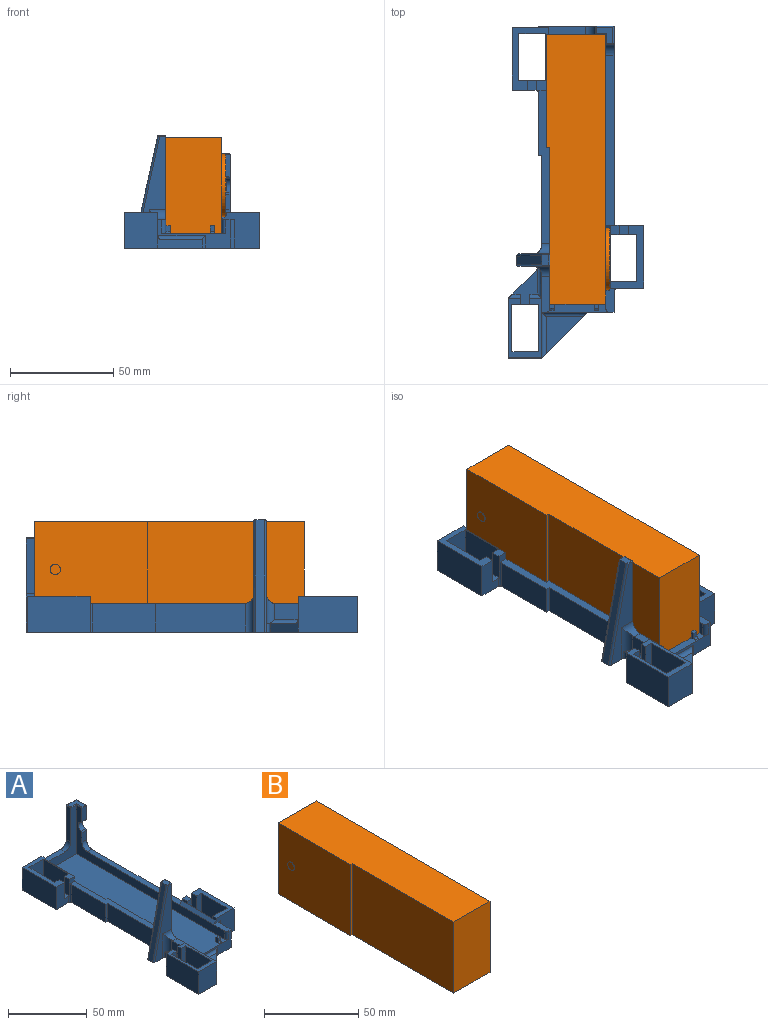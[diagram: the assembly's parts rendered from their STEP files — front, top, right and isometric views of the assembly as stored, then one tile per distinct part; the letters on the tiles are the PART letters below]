
ASSEMBLY  parts=2 mates=1
PART A: 117 faces, bbox 65.6x160.9x54.8 mm
  f0: plane 82.48x4mm, normal (0,0,1), area 329.9mm2, adj f1,f28,f41,f115
  f1: plane 96.48x45.15mm, normal (1,0,0), area 1595mm2, adj f0,f27,f31,f32,f38,f41,f47,f53
  f2: plane 17.5x11.5mm, normal (0,-1,0), area 148.3mm2, adj f4,f32,f57,f111,f113,f114
  f3: plane 12.75x4.56mm, normal (-1,0,0), area 57.9mm2, adj f5,f57,f59,f112,f113,f114
  f4: plane 12.75x4.5mm, normal (1,0,0), area 57.4mm2, adj f2,f57,f59,f113
  f5: plane 74.33x6.35mm, normal (0,0,1), area 304.3mm2, adj f3,f6,f25,f29,f30,f33,f34,f42
  f6: plane 30.85x13.75mm, normal (-1,0,0), area 424.1mm2, adj f5,f29,f32,f114
  f7: cylinder r=1mm len=54.65mm, axis (0.22,0,0.98), area 87.2mm2, adj f32,f35,f36,f50,f56
  f8: cylinder r=1mm len=54.65mm, axis (0.22,0,0.98), area 87.2mm2, adj f21,f32,f35,f52,f56
  f9: plane 4.5x1.75mm, normal (-1,0,0), area 7.9mm2, adj f11,f64,f107,f115
  f10: plane 3x1.75mm, normal (-1,0,0), area 5.3mm2, adj f12,f13,f63,f107
  f11: plane 4.5x4.15mm, normal (0,0,1), area 18.7mm2, adj f9,f64,f67,f115
  f12: plane 30.5x16mm, normal (0,0,1), area 154.7mm2, adj f10,f13,f63,f64,f65,f68,f115,f116
  f13: plane 18.3x17.5mm, normal (0,-1,0), area 231.4mm2, adj f10,f12,f17,f32,f91,f107,f116
  f14: plane 23x15.75mm, normal (1,0,0), area 362.3mm2, adj f32,f63,f64,f107
  f15: plane 3.75x3.43mm, normal (1,0,0), area 12.8mm2, adj f23,f26,f57,f60
  f16: plane 134.75x31.1mm, normal (0,0,1), area 3733.9mm2, adj f20,f25,f26,f28,f33,f34,f94,f97
  f17: plane 11.78x6mm, normal (0,0,1), area 47.1mm2, adj f13,f20,f22,f28,f91,f106
  f18: plane 17.35x4mm, normal (0,0,1), area 67.5mm2, adj f19,f20,f34,f43,f71,f80,f105
  f19: plane 11.42x7.85mm, normal (-1,0,0), area 88.5mm2, adj f18,f43,f71,f89,f108
  f20: plane 34.95x13.75mm, normal (0,-1,0), area 141mm2, adj f16,f17,f18,f22,f32,f80,f87,f90
  f21: plane 53.9x14.98mm, normal (0,-1,0), area 333.8mm2, adj f8,f32,f34,f43,f52,f108
  f22: plane 13.75x9.78mm, normal (1,0,0), area 134.4mm2, adj f17,f20,f32,f91
  f23: plane 22.8x4mm, normal (0,0,1), area 73.4mm2, adj f15,f24,f26,f31,f40,f60
  f24: plane 13.75x0.58mm, normal (-1,0,0), area 7.9mm2, adj f23,f31,f32,f60
  f25: plane 54.92x10.25mm, normal (1,0,0), area 458.5mm2, adj f5,f16,f26,f33,f57,f112
  f26: plane 37.9x28.8mm, normal (0,-1,0), area 354.1mm2, adj f15,f16,f23,f25,f28,f39,f40,f46
  f27: plane 7.26x4mm, normal (0,-1,0), area 29.1mm2, adj f1,f28,f41,f55
  f28: plane 132.75x37.9mm, normal (-1,0,0), area 1005.7mm2, adj f0,f16,f17,f26,f27,f38,f41,f44
  f29: plane 13.75x1.7mm, normal (0,-1,0), area 23.4mm2, adj f5,f6,f30,f32
  f30: plane 43.48x13.85mm, normal (-1,0,0), area 597.9mm2, adj f5,f29,f32,f42,f109
  f31: plane 45.15x36.8mm, normal (0,1,0), area 794mm2, adj f1,f23,f24,f32,f39,f40,f49
  f32: plane 160.91x65.54mm, normal (0,0,-1), area 5829.9mm2, adj f1,f2,f6,f7,f8,f13,f14,f20
  f33: plane 6.5x1.7mm, normal (0,1,0), area 11.1mm2, adj f5,f16,f25,f34
  f34: plane 77.83x46.65mm, normal (1,0,0), area 750.5mm2, adj f5,f16,f18,f21,f33,f36,f42,f43
  f35: plane 5.01x3.4mm, normal (0,0,1), area 16.9mm2, adj f7,f8,f50,f51,f52,f56
  f36: plane 53.9x14.98mm, normal (0,1,0), area 333.8mm2, adj f7,f32,f34,f42,f50,f109
  f37: plane 8x8mm, normal (0,0,1), area 39mm2, adj f44,f45,f46,f47,f48,f49
  f38: plane 10.36x4mm, normal (0,-1,0), area 41.5mm2, adj f1,f28,f45,f54
  f39: plane 26.4x4mm, normal (-1,0,0), area 105.6mm2, adj f26,f31,f40,f48
  f40: cylinder r=5mm len=5mm, axis (0,-1,0), area 31.4mm2, adj f23,f26,f31,f39
  f41: cylinder r=5mm len=5mm, axis (1,0,0), area 31.4mm2, adj f0,f1,f27,f28
  f42: cylinder r=5mm len=8mm, axis (-1,0,0), area 41.6mm2, adj f5,f30,f34,f36,f109
  f43: cylinder r=5mm len=8mm, axis (1,0,0), area 41.6mm2, adj f18,f19,f21,f34,f108
  f44: cylinder r=0.5mm len=5.5mm, axis (0,1,0), area 3.9mm2, adj f28,f37,f45,f46
  f45: cylinder r=0.5mm len=4mm, axis (-1,0,0), area 2.9mm2, adj f37,f38,f44,f47
  f46: cylinder r=0.5mm len=5.5mm, axis (-1,0,0), area 3.9mm2, adj f26,f37,f44,f48
  f47: cylinder r=0.5mm len=9mm, axis (0,1,0), area 6.8mm2, adj f1,f37,f45,f49
  f48: cylinder r=0.5mm len=4mm, axis (0,1,0), area 2.9mm2, adj f37,f39,f46,f49
  f49: cylinder r=0.5mm len=9mm, axis (-1,0,0), area 6.8mm2, adj f31,f37,f47,f48
  f50: cylinder r=0.5mm len=3.75mm, axis (1,0,0), area 2.5mm2, adj f7,f35,f36,f51
  f51: cylinder r=0.5mm len=6mm, axis (0,-1,0), area 4.4mm2, adj f34,f35,f50,f52
  f52: cylinder r=0.5mm len=3.75mm, axis (-1,0,0), area 2.5mm2, adj f8,f21,f35,f51
  f53: cylinder r=3.5mm len=6.83mm, axis (1,0,0), area 37.7mm2, adj f1,f28,f54,f55
  f54: cylinder r=1mm len=4mm, axis (1,0,0), area 5.4mm2, adj f1,f28,f38,f53
  f55: cylinder r=1mm len=4mm, axis (1,0,0), area 5.4mm2, adj f1,f27,f28,f53
  f56: plane 54.4x12.11mm, normal (-0.98,0,0.22), area 222.9mm2, adj f7,f8,f32,f35
  f57: plane 30.5x17.7mm, normal (0,0,1), area 192.7mm2, adj f2,f3,f4,f15,f25,f26,f58,f59
  f58: plane 17.5x12.8mm, normal (0,-1,0), area 224mm2, adj f32,f57,f61,f62
  f59: plane 17.5x12.8mm, normal (0,1,0), area 166.6mm2, adj f3,f4,f32,f57,f61,f62,f113
  f60: plane 17.7x17.5mm, normal (0,1,0), area 238.3mm2, adj f15,f23,f24,f32,f57,f111
  f61: plane 23x17.5mm, normal (-1,0,0), area 402.5mm2, adj f32,f57,f58,f59
  f62: plane 23x17.5mm, normal (1,0,0), area 402.5mm2, adj f32,f57,f58,f59
  f63: plane 17.5x12.8mm, normal (0,1,0), area 224mm2, adj f10,f12,f14,f32,f65
  f64: plane 17.5x12.8mm, normal (0,-1,0), area 163.2mm2, adj f9,f11,f12,f14,f32,f65,f66,f67
  f65: plane 23x17.5mm, normal (-1,0,0), area 402.5mm2, adj f12,f32,f63,f64
  f66: plane 4.5x4.5mm, normal (0,0,1), area 20.2mm2, adj f64,f67,f68,f115
  f67: plane 13.5x4.5mm, normal (1,0,0), area 60.7mm2, adj f11,f64,f66,f115
  f68: plane 13.5x4.5mm, normal (-1,0,0), area 60.7mm2, adj f12,f64,f66,f115
  f69: plane 18.26x12.05mm, normal (0,0,1), area 95.4mm2, adj f70,f73,f81,f82,f85,f88,f89,f108
  f70: plane 13.59x13.59mm, normal (-0.71,0.71,0), area 78.1mm2, adj f32,f69,f77,f85,f110
  f71: plane 11.5x5.85mm, normal (0,1,0), area 66.1mm2, adj f18,f19,f72,f80,f82,f88
  f72: plane 29x16.2mm, normal (0,0,1), area 161.9mm2, adj f71,f73,f74,f75,f76,f77,f78,f79
  f73: plane 17.5x12.8mm, normal (0,-1,0), area 163.2mm2, adj f32,f69,f72,f78,f79,f81,f82
  f74: plane 17.5x16.2mm, normal (0,-1,0), area 283.5mm2, adj f32,f72,f77,f80,f84
  f75: plane 17.5x12.8mm, normal (0,1,0), area 224mm2, adj f32,f72,f78,f79
  f76: plane 11.5x5.85mm, normal (0,1,0), area 67.3mm2, adj f72,f77,f81,f85
  f77: plane 29x17.5mm, normal (-1,0,0), area 507.5mm2, adj f32,f70,f72,f74,f76
  f78: plane 23x17.5mm, normal (-1,0,0), area 402.5mm2, adj f32,f72,f73,f75
  f79: plane 23x17.5mm, normal (1,0,0), area 402.5mm2, adj f32,f72,f73,f75
  f80: plane 29x11.5mm, normal (1,0,0), area 279.8mm2, adj f18,f20,f71,f72,f74,f86
  f81: plane 13.5x5mm, normal (1,0,0), area 41.4mm2, adj f69,f72,f73,f76,f85
  f82: plane 13.5x5mm, normal (-1,0,0), area 41.4mm2, adj f69,f71,f72,f73,f88
  f83: plane 18.07x18.07mm, normal (0,0,1), area 163.3mm2, adj f84,f86,f87
  f84: plane 21.6x21.6mm, normal (0.71,-0.71,0), area 123.1mm2, adj f32,f74,f83,f86,f87,f90
  f85: cylinder r=2mm len=5.85mm, axis (1,0,0), area 16.1mm2, adj f69,f70,f76,f81
  f86: cylinder r=2mm len=22.07mm, axis (0,-1,0), area 64.8mm2, adj f80,f83,f84,f87
  f87: cylinder r=2mm len=22.9mm, axis (-1,0,0), area 65.2mm2, adj f20,f83,f84,f86,f90
  f88: cylinder r=2mm len=5.7mm, axis (1,0,0), area 15.6mm2, adj f69,f71,f82,f89
  f89: cylinder r=2mm len=14.88mm, axis (0,1,0), area 39.8mm2, adj f19,f69,f88,f108
  f90: cylinder r=2mm len=6mm, axis (0,0,-1), area 8.3mm2, adj f20,f32,f84,f87
  f91: cylinder r=2mm len=13.75mm, axis (0,0,1), area 43.2mm2, adj f13,f17,f22,f32
  f92: plane 3.4x2.15mm, normal (0,1,0), area 7.3mm2, adj f34,f94,f95,f104
  f93: plane 2.5x2.15mm, normal (0,-1,0), area 5.4mm2, adj f94,f95,f102,f105
  f94: plane 3.5x3.1mm, normal (1,0,0), area 7.2mm2, adj f16,f92,f93,f95,f102,f104
  f95: plane 2.15x2mm, normal (0,0,1), area 4.3mm2, adj f34,f92,f93,f94
  f96: plane 3.4x2mm, normal (0,1,0), area 6.8mm2, adj f97,f99,f100,f103
  f97: plane 3.5x3.1mm, normal (-1,0,0), area 7.2mm2, adj f16,f96,f98,f100,f101,f103
  f98: plane 2.5x2mm, normal (0,-1,0), area 5mm2, adj f97,f99,f100,f101
  f99: plane 3.5x3.1mm, normal (1,0,0), area 7.2mm2, adj f16,f96,f98,f100,f101,f103
  f100: plane 2x2mm, normal (0,0,1), area 4mm2, adj f96,f97,f98,f99
  f101: cylinder r=1mm len=2mm, axis (1,0,0), area 3.1mm2, adj f16,f97,f98,f99
  f102: cylinder r=1mm len=2.42mm, axis (1,0,0), area 3.5mm2, adj f16,f93,f94,f105
  f103: cylinder r=0.1mm len=2mm, axis (-1,0,0), area 0.3mm2, adj f16,f96,f97,f99
  f104: cylinder r=0.1mm len=2.15mm, axis (-1,0,0), area 0.3mm2, adj f16,f34,f92,f94
  f105: cylinder r=2mm len=6.5mm, axis (0,0,1), area 20.2mm2, adj f16,f18,f20,f34,f93,f102
  f106: cylinder r=2mm len=6.5mm, axis (0,0,1), area 20.4mm2, adj f16,f17,f20,f28
  f107: plane 30.5x2.3mm, normal (-0.66,0,0.75), area 93mm2, adj f9,f10,f13,f14,f28,f115
  f108: cylinder r=4mm len=18.75mm, axis (0,0,-1), area 75.5mm2, adj f19,f21,f32,f43,f69,f89,f110
  f109: cylinder r=4mm len=18.75mm, axis (0,0,-1), area 99.2mm2, adj f30,f32,f36,f42
  f110: cylinder r=1mm len=4mm, axis (0,0,-1), area 8.3mm2, adj f32,f69,f70,f108
  f111: plane 30.5x17.5mm, normal (-1,0,0), area 533.8mm2, adj f2,f32,f57,f60
  f112: plane 4.65x3.75mm, normal (0,-1,0), area 17.4mm2, adj f3,f5,f25,f57
  f113: plane 4.56x4.5mm, normal (0,0,1), area 20.3mm2, adj f2,f3,f4,f59,f114
  f114: cylinder r=1mm len=13.75mm, axis (0,0,-1), area 18.4mm2, adj f2,f3,f5,f6,f32,f113
  f115: plane 18.3x17.5mm, normal (0,1,0), area 198.2mm2, adj f0,f1,f9,f11,f12,f32,f66,f67
  f116: plane 30.5x17.5mm, normal (1,0,0), area 533.8mm2, adj f12,f13,f32,f115
PART B: 14 faces, bbox 31.1x130.6x46.2 mm
  f0: plane 46.2x28.6mm, normal (0,1,0), area 1321.3mm2, adj f1,f5,f6,f7
  f1: plane 54.65x46.2mm, normal (-1,0,0), area 2505.2mm2, adj f0,f2,f6,f7,f8
  f2: plane 46.2x1.5mm, normal (0,-1,0), area 69.3mm2, adj f1,f3,f6,f7
  f3: plane 75.95x46.2mm, normal (-1,0,0), area 3508.9mm2, adj f2,f4,f6,f7
  f4: plane 46.2x27.1mm, normal (0,-1,0), area 1252mm2, adj f3,f5,f6,f7
  f5: plane 130.6x46.2mm, normal (1,0,0), area 5317.4mm2, adj f0,f4,f6,f7,f10
  f6: plane 130.6x28.6mm, normal (0,0,1), area 3621.2mm2, adj f0,f1,f2,f3,f4,f5
  f7: plane 130.6x28.6mm, normal (0,0,-1), area 3621.2mm2, adj f0,f1,f2,f3,f4,f5
  f8: cylinder r=2.5mm len=5mm, axis (1,0,0), area 3.9mm2, adj f1,f9
  f9: plane 5x5mm, normal (-1,0,0), area 19.6mm2, adj f8
  f10: cylinder r=15.1mm len=30.2mm, axis (-1,0,0), area 180.3mm2, adj f5,f11
  f11: plane 30.2x30.2mm, normal (1,0,0), area 696.7mm2, adj f10,f12
  f12: cylinder r=2.5mm len=5mm, axis (-1,0,0), area 4.7mm2, adj f11,f13
  f13: plane 5x5mm, normal (1,0,0), area 19.6mm2, adj f12
PLACE A t=(-13.49,58.76,-32.04)mm
PLACE B t=(-13.49,58.76,-32.04)mm
MATE fastened B.f7 <-> A.f16  axis (0,0,-1) through (-13.49,58.76,-32.04)mm
